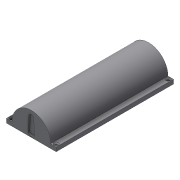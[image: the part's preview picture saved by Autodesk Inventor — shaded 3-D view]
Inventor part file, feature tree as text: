
AUTODESK INVENTOR PART (.ipt)
format: ipt  version: 2021 (Build 250183000, 183)  size: 129,024 bytes
history: native  units: mm
features: sketch x3, extrude x2, projected_geometry x2, other x1, hole x1
ambient origin geometry x8: Origin, YZ Plane, XZ Plane, XY Plane, X Axis, Y Axis, Z Axis, Center Point
bodies: Body1 (feature_tree)
feature tree (9):
  other  "Твердое тело1"
  extrude  "Выдавливание1"  Depth=8.0mm
  extrude  "Выдавливание2"  Depth=6.0mm
  hole  "Отверстие1"  [1 undecoded]
  sketch  "Эскиз1"
  sketch  "Эскиз2"
  projected_geometry  "Спроецированная петля1"
  sketch  "Эскиз3"
  projected_geometry  "Спроецированная петля2"
note: 1 required parameter value undecoded (feature->parameter linkage not recoverable at this tier; creation-order binding heuristic only, values carry confidence <= 0.55)
